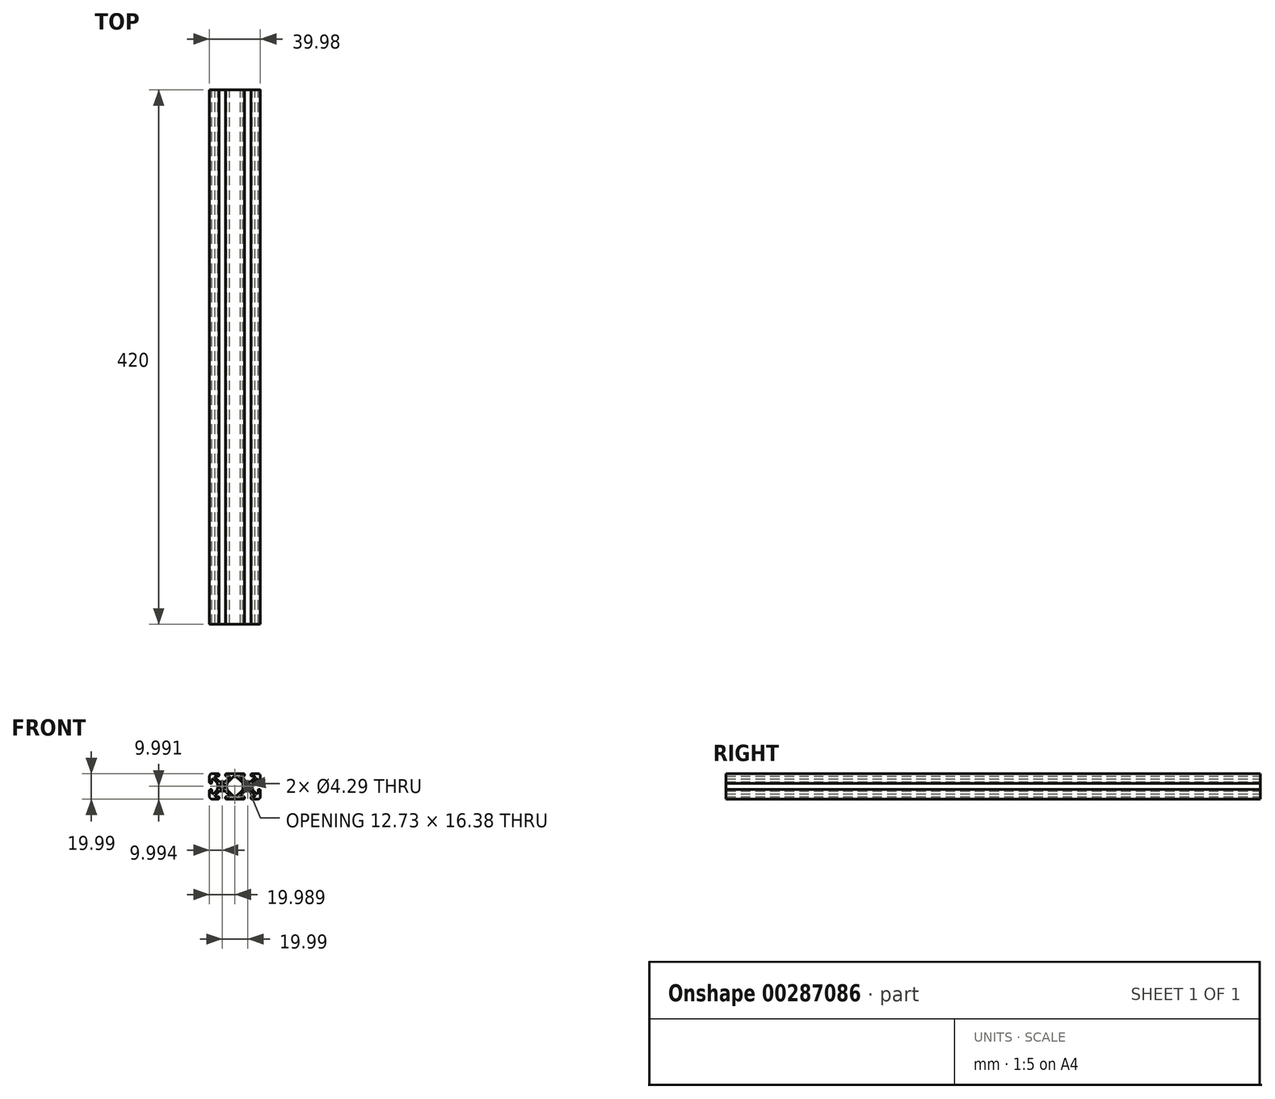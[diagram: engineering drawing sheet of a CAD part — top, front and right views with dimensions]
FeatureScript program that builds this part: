
annotation { "Feature Type Name" : "Feature", "Feature Type Description" : "" }
export const myFeature = defineFeature(function(context is Context, id is Id, definition is map)
    precondition{}
    {
        {
            var Q0;
            Q0=qCreatedBy(makeId("Front.planeOp"),FACE);
            var sketch = newSketch(context, id + "F0", { "sketchPlane" : qUnion([Q0])});
            skArc(sketch, "E0.0.0", {"start": v(-12.02, 4.76) * mm, "mid": v(-13.17, 4.99) * mm, "end": v(-14.14, 5.64) * mm});
            skLineSegment(sketch, "E0.0.1", {"start": v(-14.14, 5.64) * mm, "end": v(-16.4, 7.9) * mm});
            skArc(sketch, "E0.0.2", {"start": v(-16.4, 7.9) * mm, "mid": v(-16.58, 8.8) * mm, "end": v(-15.8, 9.32) * mm});
            skLineSegment(sketch, "E0.0.3", {"start": v(-15.8, 9.32) * mm, "end": v(-13.7, 9.32) * mm});
            skArc(sketch, "E0.0.4", {"start": v(-13.7, 9.32) * mm, "mid": v(-13.48, 9.41) * mm, "end": v(-13.39, 9.63) * mm});
            skLineSegment(sketch, "E0.0.5", {"start": v(-13.39, 9.63) * mm, "end": v(-13.39, 10.34) * mm});
            skArc(sketch, "E0.0.6", {"start": v(-13.39, 10.34) * mm, "mid": v(-13.62, 10.9) * mm, "end": v(-14.18, 11.13) * mm});
            skLineSegment(sketch, "E0.0.7", {"start": v(-14.18, 11.13) * mm, "end": v(-18.87, 11.13) * mm});
            skArc(sketch, "E0.0.8", {"start": v(-18.87, 11.13) * mm, "mid": v(-20.3, 10.54) * mm, "end": v(-20.88, 9.12) * mm});
            skLineSegment(sketch, "E0.0.9", {"start": v(-20.88, 9.12) * mm, "end": v(-20.88, 4.42) * mm});
            skArc(sketch, "E0.0.10", {"start": v(-20.88, 4.42) * mm, "mid": v(-20.65, 3.86) * mm, "end": v(-20.1, 3.63) * mm});
            skLineSegment(sketch, "E0.0.11", {"start": v(-20.1, 3.63) * mm, "end": v(-19.38, 3.63) * mm});
            skArc(sketch, "E0.0.12", {"start": v(-19.38, 3.63) * mm, "mid": v(-19.17, 3.72) * mm, "end": v(-19.08, 3.94) * mm});
            skLineSegment(sketch, "E0.0.13", {"start": v(-19.08, 3.94) * mm, "end": v(-19.08, 6.05) * mm});
            skArc(sketch, "E0.0.14", {"start": v(-19.08, 6.05) * mm, "mid": v(-18.56, 6.82) * mm, "end": v(-17.65, 6.64) * mm});
            skLineSegment(sketch, "E0.0.15", {"start": v(-17.65, 6.64) * mm, "end": v(-15.4, 4.38) * mm});
            skArc(sketch, "E0.0.16", {"start": v(-15.4, 4.38) * mm, "mid": v(-14.74, 3.41) * mm, "end": v(-14.51, 2.26) * mm});
            skLineSegment(sketch, "E0.0.17", {"start": v(-14.51, 2.26) * mm, "end": v(-14.51, 0) * mm});
            skArc(sketch, "E0.0.18", {"start": v(-14.51, 0) * mm, "mid": v(-14.74, -1.15) * mm, "end": v(-15.4, -2.12) * mm});
            skLineSegment(sketch, "E0.0.19", {"start": v(-15.4, -2.12) * mm, "end": v(-17.65, -4.38) * mm});
            skArc(sketch, "E0.0.20", {"start": v(-17.65, -4.38) * mm, "mid": v(-18.56, -4.56) * mm, "end": v(-19.08, -3.78) * mm});
            skLineSegment(sketch, "E0.0.21", {"start": v(-19.08, -3.78) * mm, "end": v(-19.08, -1.68) * mm});
            skArc(sketch, "E0.0.22", {"start": v(-19.08, -1.68) * mm, "mid": v(-19.17, -1.46) * mm, "end": v(-19.38, -1.37) * mm});
            skLineSegment(sketch, "E0.0.23", {"start": v(-19.38, -1.37) * mm, "end": v(-20.1, -1.37) * mm});
            skArc(sketch, "E0.0.24", {"start": v(-20.1, -1.37) * mm, "mid": v(-20.65, -1.6) * mm, "end": v(-20.88, -2.16) * mm});
            skLineSegment(sketch, "E0.0.25", {"start": v(-20.88, -2.16) * mm, "end": v(-20.88, -6.86) * mm});
            skArc(sketch, "E0.0.26", {"start": v(-20.88, -6.86) * mm, "mid": v(-20.3, -8.28) * mm, "end": v(-18.87, -8.86) * mm});
            skLineSegment(sketch, "E0.0.27", {"start": v(-18.87, -8.86) * mm, "end": v(-14.18, -8.86) * mm});
            skArc(sketch, "E0.0.28", {"start": v(-14.18, -8.86) * mm, "mid": v(-13.62, -8.63) * mm, "end": v(-13.39, -8.08) * mm});
            skLineSegment(sketch, "E0.0.29", {"start": v(-13.39, -8.08) * mm, "end": v(-13.39, -7.36) * mm});
            skArc(sketch, "E0.0.30", {"start": v(-13.39, -7.36) * mm, "mid": v(-13.48, -7.15) * mm, "end": v(-13.7, -7.06) * mm});
            skLineSegment(sketch, "E0.0.31", {"start": v(-13.7, -7.06) * mm, "end": v(-15.8, -7.06) * mm});
            skArc(sketch, "E0.0.32", {"start": v(-15.8, -7.06) * mm, "mid": v(-16.58, -6.54) * mm, "end": v(-16.4, -5.63) * mm});
            skLineSegment(sketch, "E0.0.33", {"start": v(-16.4, -5.63) * mm, "end": v(-14.14, -3.37) * mm});
            skArc(sketch, "E0.0.34", {"start": v(-14.14, -3.37) * mm, "mid": v(-13.17, -2.72) * mm, "end": v(-12.02, -2.5) * mm});
            skLineSegment(sketch, "E0.0.35", {"start": v(-12.02, -2.5) * mm, "end": v(-9.75, -2.5) * mm});
            skArc(sketch, "E0.0.36", {"start": v(-9.75, -2.5) * mm, "mid": v(-8.6, -2.72) * mm, "end": v(-7.63, -3.37) * mm});
            skLineSegment(sketch, "E0.0.37", {"start": v(-7.63, -3.37) * mm, "end": v(-5.38, -5.63) * mm});
            skArc(sketch, "E0.0.38", {"start": v(-5.38, -5.63) * mm, "mid": v(-5.2, -6.54) * mm, "end": v(-5.97, -7.06) * mm});
            skLineSegment(sketch, "E0.0.39", {"start": v(-5.97, -7.06) * mm, "end": v(-8.08, -7.06) * mm});
            skArc(sketch, "E0.0.40", {"start": v(-8.08, -7.06) * mm, "mid": v(-8.3, -7.15) * mm, "end": v(-8.38, -7.36) * mm});
            skLineSegment(sketch, "E0.0.41", {"start": v(-8.38, -7.36) * mm, "end": v(-8.38, -8.08) * mm});
            skArc(sketch, "E0.0.42", {"start": v(-8.38, -8.08) * mm, "mid": v(-8.15, -8.63) * mm, "end": v(-7.6, -8.86) * mm});
            skLineSegment(sketch, "E0.0.43", {"start": v(-7.6, -8.86) * mm, "end": v(5.81, -8.86) * mm});
            skArc(sketch, "E0.0.44", {"start": v(5.81, -8.86) * mm, "mid": v(6.37, -8.63) * mm, "end": v(6.6, -8.08) * mm});
            skLineSegment(sketch, "E0.0.45", {"start": v(6.6, -8.08) * mm, "end": v(6.6, -7.36) * mm});
            skArc(sketch, "E0.0.46", {"start": v(6.6, -7.36) * mm, "mid": v(6.51, -7.15) * mm, "end": v(6.3, -7.06) * mm});
            skLineSegment(sketch, "E0.0.47", {"start": v(6.3, -7.06) * mm, "end": v(4.19, -7.06) * mm});
            skArc(sketch, "E0.0.48", {"start": v(4.19, -7.06) * mm, "mid": v(3.41, -6.54) * mm, "end": v(3.6, -5.63) * mm});
            skLineSegment(sketch, "E0.0.49", {"start": v(3.6, -5.63) * mm, "end": v(5.85, -3.37) * mm});
            skArc(sketch, "E0.0.50", {"start": v(5.85, -3.37) * mm, "mid": v(6.82, -2.72) * mm, "end": v(7.97, -2.5) * mm});
            skLineSegment(sketch, "E0.0.51", {"start": v(7.97, -2.5) * mm, "end": v(10.24, -2.5) * mm});
            skArc(sketch, "E0.0.52", {"start": v(10.24, -2.5) * mm, "mid": v(11.38, -2.72) * mm, "end": v(12.36, -3.37) * mm});
            skLineSegment(sketch, "E0.0.53", {"start": v(12.36, -3.37) * mm, "end": v(14.61, -5.63) * mm});
            skArc(sketch, "E0.0.54", {"start": v(14.61, -5.63) * mm, "mid": v(14.8, -6.54) * mm, "end": v(14.02, -7.06) * mm});
            skLineSegment(sketch, "E0.0.55", {"start": v(14.02, -7.06) * mm, "end": v(11.91, -7.06) * mm});
            skArc(sketch, "E0.0.56", {"start": v(11.91, -7.06) * mm, "mid": v(11.7, -7.15) * mm, "end": v(11.6, -7.36) * mm});
            skLineSegment(sketch, "E0.0.57", {"start": v(11.6, -7.36) * mm, "end": v(11.6, -8.08) * mm});
            skArc(sketch, "E0.0.58", {"start": v(11.6, -8.08) * mm, "mid": v(11.84, -8.63) * mm, "end": v(12.4, -8.86) * mm});
            skLineSegment(sketch, "E0.0.59", {"start": v(12.4, -8.86) * mm, "end": v(17.1, -8.86) * mm});
            skArc(sketch, "E0.0.60", {"start": v(17.1, -8.86) * mm, "mid": v(18.51, -8.28) * mm, "end": v(19.1, -6.86) * mm});
            skLineSegment(sketch, "E0.0.61", {"start": v(19.1, -6.86) * mm, "end": v(19.1, -2.16) * mm});
            skArc(sketch, "E0.0.62", {"start": v(19.1, -2.16) * mm, "mid": v(18.87, -1.6) * mm, "end": v(18.31, -1.37) * mm});
            skLineSegment(sketch, "E0.0.63", {"start": v(18.31, -1.37) * mm, "end": v(17.6, -1.37) * mm});
            skArc(sketch, "E0.0.64", {"start": v(17.6, -1.37) * mm, "mid": v(17.38, -1.46) * mm, "end": v(17.3, -1.68) * mm});
            skLineSegment(sketch, "E0.0.65", {"start": v(17.3, -1.68) * mm, "end": v(17.3, -3.78) * mm});
            skArc(sketch, "E0.0.66", {"start": v(17.3, -3.78) * mm, "mid": v(16.78, -4.56) * mm, "end": v(15.86, -4.38) * mm});
            skLineSegment(sketch, "E0.0.67", {"start": v(15.86, -4.38) * mm, "end": v(13.6, -2.12) * mm});
            skArc(sketch, "E0.0.68", {"start": v(13.6, -2.12) * mm, "mid": v(12.96, -1.15) * mm, "end": v(12.73, 0) * mm});
            skLineSegment(sketch, "E0.0.69", {"start": v(12.73, 0) * mm, "end": v(12.73, 2.26) * mm});
            skArc(sketch, "E0.0.70", {"start": v(12.73, 2.26) * mm, "mid": v(12.96, 3.41) * mm, "end": v(13.6, 4.38) * mm});
            skLineSegment(sketch, "E0.0.71", {"start": v(13.6, 4.38) * mm, "end": v(15.86, 6.64) * mm});
            skArc(sketch, "E0.0.72", {"start": v(15.86, 6.64) * mm, "mid": v(16.78, 6.82) * mm, "end": v(17.3, 6.05) * mm});
            skLineSegment(sketch, "E0.0.73", {"start": v(17.3, 6.05) * mm, "end": v(17.3, 3.94) * mm});
            skArc(sketch, "E0.0.74", {"start": v(17.3, 3.94) * mm, "mid": v(17.38, 3.72) * mm, "end": v(17.6, 3.63) * mm});
            skLineSegment(sketch, "E0.0.75", {"start": v(17.6, 3.63) * mm, "end": v(18.31, 3.63) * mm});
            skArc(sketch, "E0.0.76", {"start": v(18.31, 3.63) * mm, "mid": v(18.87, 3.86) * mm, "end": v(19.1, 4.42) * mm});
            skLineSegment(sketch, "E0.0.77", {"start": v(19.1, 4.42) * mm, "end": v(19.1, 9.12) * mm});
            skArc(sketch, "E0.0.78", {"start": v(19.1, 9.12) * mm, "mid": v(18.51, 10.54) * mm, "end": v(17.1, 11.13) * mm});
            skLineSegment(sketch, "E0.0.79", {"start": v(17.1, 11.13) * mm, "end": v(12.4, 11.13) * mm});
            skArc(sketch, "E0.0.80", {"start": v(12.4, 11.13) * mm, "mid": v(11.84, 10.9) * mm, "end": v(11.6, 10.34) * mm});
            skLineSegment(sketch, "E0.0.81", {"start": v(11.6, 10.34) * mm, "end": v(11.6, 9.63) * mm});
            skArc(sketch, "E0.0.82", {"start": v(11.6, 9.63) * mm, "mid": v(11.7, 9.41) * mm, "end": v(11.91, 9.32) * mm});
            skLineSegment(sketch, "E0.0.83", {"start": v(11.91, 9.32) * mm, "end": v(14.02, 9.32) * mm});
            skArc(sketch, "E0.0.84", {"start": v(14.02, 9.32) * mm, "mid": v(14.8, 8.8) * mm, "end": v(14.61, 7.9) * mm});
            skLineSegment(sketch, "E0.0.85", {"start": v(14.61, 7.9) * mm, "end": v(12.36, 5.64) * mm});
            skArc(sketch, "E0.0.86", {"start": v(12.36, 5.64) * mm, "mid": v(11.38, 4.99) * mm, "end": v(10.24, 4.76) * mm});
            skLineSegment(sketch, "E0.0.87", {"start": v(10.24, 4.76) * mm, "end": v(7.97, 4.76) * mm});
            skArc(sketch, "E0.0.88", {"start": v(7.97, 4.76) * mm, "mid": v(6.82, 4.99) * mm, "end": v(5.85, 5.64) * mm});
            skLineSegment(sketch, "E0.0.89", {"start": v(5.85, 5.64) * mm, "end": v(3.6, 7.9) * mm});
            skArc(sketch, "E0.0.90", {"start": v(3.6, 7.9) * mm, "mid": v(3.41, 8.8) * mm, "end": v(4.19, 9.32) * mm});
            skLineSegment(sketch, "E0.0.91", {"start": v(4.19, 9.32) * mm, "end": v(6.3, 9.32) * mm});
            skArc(sketch, "E0.0.92", {"start": v(6.3, 9.32) * mm, "mid": v(6.51, 9.41) * mm, "end": v(6.6, 9.63) * mm});
            skLineSegment(sketch, "E0.0.93", {"start": v(6.6, 9.63) * mm, "end": v(6.6, 10.34) * mm});
            skArc(sketch, "E0.0.94", {"start": v(6.6, 10.34) * mm, "mid": v(6.37, 10.9) * mm, "end": v(5.81, 11.13) * mm});
            skLineSegment(sketch, "E0.0.95", {"start": v(5.81, 11.13) * mm, "end": v(-7.6, 11.13) * mm});
            skArc(sketch, "E0.0.96", {"start": v(-7.6, 11.13) * mm, "mid": v(-8.15, 10.9) * mm, "end": v(-8.38, 10.34) * mm});
            skLineSegment(sketch, "E0.0.97", {"start": v(-8.38, 10.34) * mm, "end": v(-8.38, 9.63) * mm});
            skArc(sketch, "E0.0.98", {"start": v(-8.38, 9.63) * mm, "mid": v(-8.3, 9.41) * mm, "end": v(-8.08, 9.32) * mm});
            skLineSegment(sketch, "E0.0.99", {"start": v(-8.08, 9.32) * mm, "end": v(-5.97, 9.32) * mm});
            skArc(sketch, "E0.0.100", {"start": v(-5.97, 9.32) * mm, "mid": v(-5.2, 8.8) * mm, "end": v(-5.38, 7.9) * mm});
            skLineSegment(sketch, "E0.0.101", {"start": v(-5.38, 7.9) * mm, "end": v(-7.63, 5.64) * mm});
            skArc(sketch, "E0.0.102", {"start": v(-7.63, 5.64) * mm, "mid": v(-8.6, 4.99) * mm, "end": v(-9.75, 4.76) * mm});
            skLineSegment(sketch, "E0.0.103", {"start": v(-9.75, 4.76) * mm, "end": v(-12.02, 4.76) * mm});
            skCircle(sketch, "E1.0", {"center": v(-10.89, 1.13) * mm, "radius": 2.15 * mm});
            skCircle(sketch, "E2.0", {"center": v(9.1, 1.13) * mm, "radius": 2.15 * mm});
            skLineSegment(sketch, "E3.0", {"start": v(-7.26, 2.26) * mm, "end": v(-7.26, 0) * mm});
            skArc(sketch, "E3.1", {"start": v(-6.38, 4.38) * mm, "mid": v(-7.03, 3.41) * mm, "end": v(-7.26, 2.26) * mm});
            skLineSegment(sketch, "E3.2", {"start": v(-1.83, 8.93) * mm, "end": v(-6.38, 4.38) * mm});
            skArc(sketch, "E3.3", {"start": v(-7.26, 0) * mm, "mid": v(-7.03, -1.15) * mm, "end": v(-6.38, -2.12) * mm});
            skLineSegment(sketch, "E3.4", {"start": v(-6.38, -2.12) * mm, "end": v(-1.83, -6.67) * mm});
            skArc(sketch, "E3.5", {"start": v(-1.83, -6.67) * mm, "mid": v(-0.9, -7.06) * mm, "end": v(0.05, -6.67) * mm});
            skLineSegment(sketch, "E3.6", {"start": v(0.05, -6.67) * mm, "end": v(4.6, -2.12) * mm});
            skLineSegment(sketch, "E3.7", {"start": v(4.6, 4.38) * mm, "end": v(0.05, 8.93) * mm});
            skLineSegment(sketch, "E3.8", {"start": v(5.48, 0) * mm, "end": v(5.48, 2.26) * mm});
            skArc(sketch, "E3.9", {"start": v(5.48, 2.26) * mm, "mid": v(5.25, 3.41) * mm, "end": v(4.6, 4.38) * mm});
            skArc(sketch, "E3.10", {"start": v(4.6, -2.12) * mm, "mid": v(5.25, -1.15) * mm, "end": v(5.48, 0) * mm});
            skArc(sketch, "E3.11", {"start": v(0.05, 8.93) * mm, "mid": v(-0.9, 9.32) * mm, "end": v(-1.83, 8.93) * mm});
            skSolve(sketch);
        }
        {
            var Q0;
            Q0=qSketchRegion(id+"F0",true);
            extrude(context, id + "F1", {"entities" : qUnion([Q0]), "depth" : 420 * mm});
        }
    });
